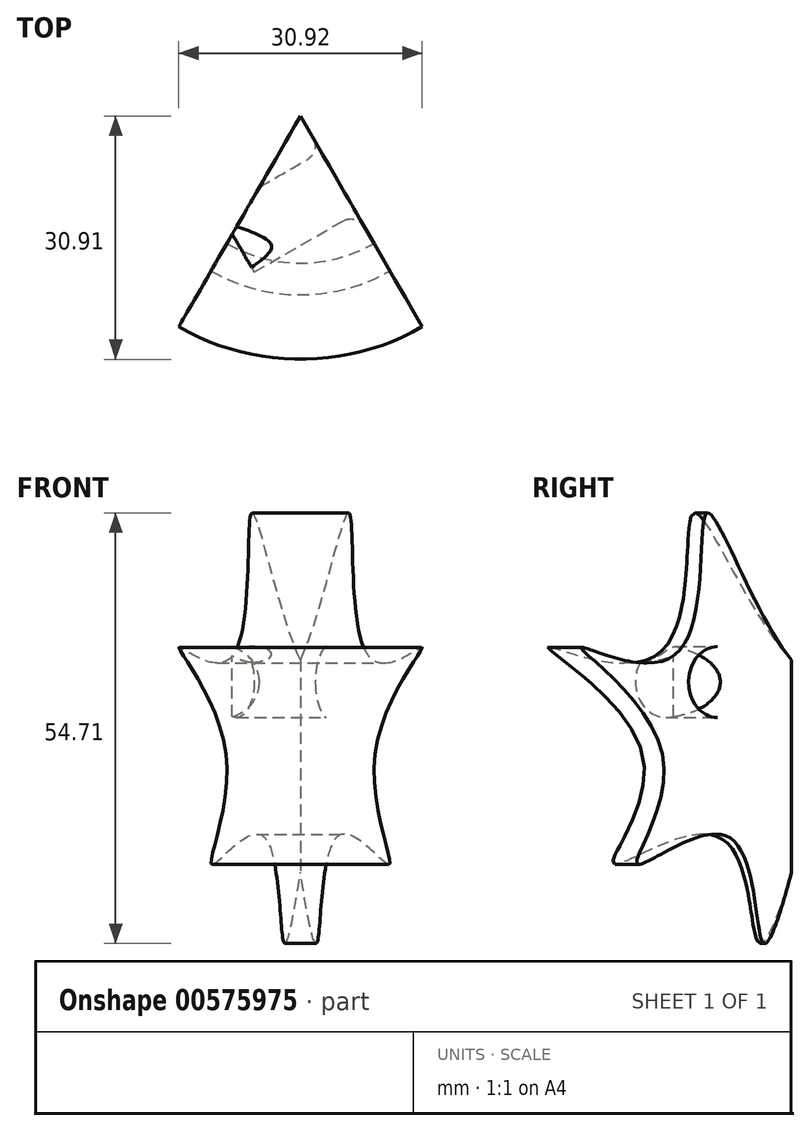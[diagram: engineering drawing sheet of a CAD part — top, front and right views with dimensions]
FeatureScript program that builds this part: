
annotation { "Feature Type Name" : "Feature", "Feature Type Description" : "" }
export const myFeature = defineFeature(function(context is Context, id is Id, definition is map)
    precondition{}
    {
        {
            var Q0;
            Q0=qCreatedBy(makeId("Right.planeOp"),FACE);
            var sketch = newSketch(context, id + "F0", { "sketchPlane" : qUnion([Q0])});
            skLineSegment(sketch, "E0", {"start": v(0, 27) * mm, "end": v(0, 0) * mm});
            skFitSpline(sketch, "E1", {"points": [v(0, 27) * mm, v(-12.47, 45.61) * mm, v(-16.94, 27.74) * mm, v(-30.9, 28.58) * mm, v(-18.86, 14.64) * mm, v(-22.57, 1.02) * mm, v(-9.14, 4.43) * mm, v(-4.2, -8.91) * mm, v(0, 0) * mm], "startDerivative": vector(-109.68, 112.83) * mm, "endDerivative": vector(43.43, 143.27) * mm});
            skSolve(sketch);
        }
        {
            var Q0;
            Q0=makeQuery(id+"F0.imprint","IMPRINT",FACE,{"disambiguationData":[TD([[makeQuery(id+"F0.imprint","IMPRINT",EDGE,{"derivedFrom":sQuery(id+"F0.wireOp",EDGE,"E0")}),-1.0]])]});
            var Q1;
            Q1=sQuery(id+"F0.wireOp",EDGE,"E0");
            revolve(context, id + "F1", {"entities" : qUnion([Q0]), "axis" : qUnion([Q1]), "revolveType" : RevolveType.TWO_DIRECTIONS, "angle" : 30 * degree, "angleBack" : 330 * degree});
        }
        {
            var Q0;
            Q0=makeQuery(id+"F1.opRevolve","CAP_FACE",FACE,{"disambiguationData":[OSD([sQuery(id+"F0.wireOp",EDGE,"E0"),sQuery(id+"F0.wireOp",EDGE,"E1")])],"isStart":true});
            var sketch = newSketch(context, id + "F2", { "sketchPlane" : qUnion([Q0])});
            skCircle(sketch, "E2", {"center": v(-9.73, 24.18) * mm, "radius": 4.5 * mm});
            skCircle(sketch, "E3", {"center": v(-6.55, 11.31) * mm, "radius": 3.05 * mm});
            skSolve(sketch);
        }
        {
            var Q0;
            Q0=makeQuery(id+"F2.imprint","IMPRINT",FACE,{"disambiguationData":[TD([[makeQuery(id+"F2.imprint","IMPRINT",EDGE,{"derivedFrom":sQuery(id+"F2.wireOp",EDGE,"E2")}),1.0]])]});
            extrude(context, id + "F3", {"entities" : qUnion([Q0]), "operationType" : NewBodyOperationType.REMOVE, "endBound" : BoundingType.SYMMETRIC, "oppositeDirection" : true, "depth" : 30 * mm, "offsetDistance" : 25 * mm});
        }
        {
            var Q0;
            Q0=makeQuery(id+"F3.boolean.opBoolean","INTERSECT",EDGE,{"derivedFrom":[makeQuery(id+"F1.opRevolve","CAP_FACE",FACE,{"disambiguationData":[OSD([sQuery(id+"F0.wireOp",EDGE,"E0"),sQuery(id+"F0.wireOp",EDGE,"E1")])],"isStart":true}),makeQuery(id+"F3.opExtrude","SWEPT_FACE",FACE,{"disambiguationData":[OSD([sQuery(id+"F2.wireOp",EDGE,"E2")])]})]});
            fillet(context, id + "F4", {"entities" : qUnion([Q0]), "radius" : 2 * mm, "tangentPropagation" : true, "allowEdgeOverflow" : false});
        }
    });
